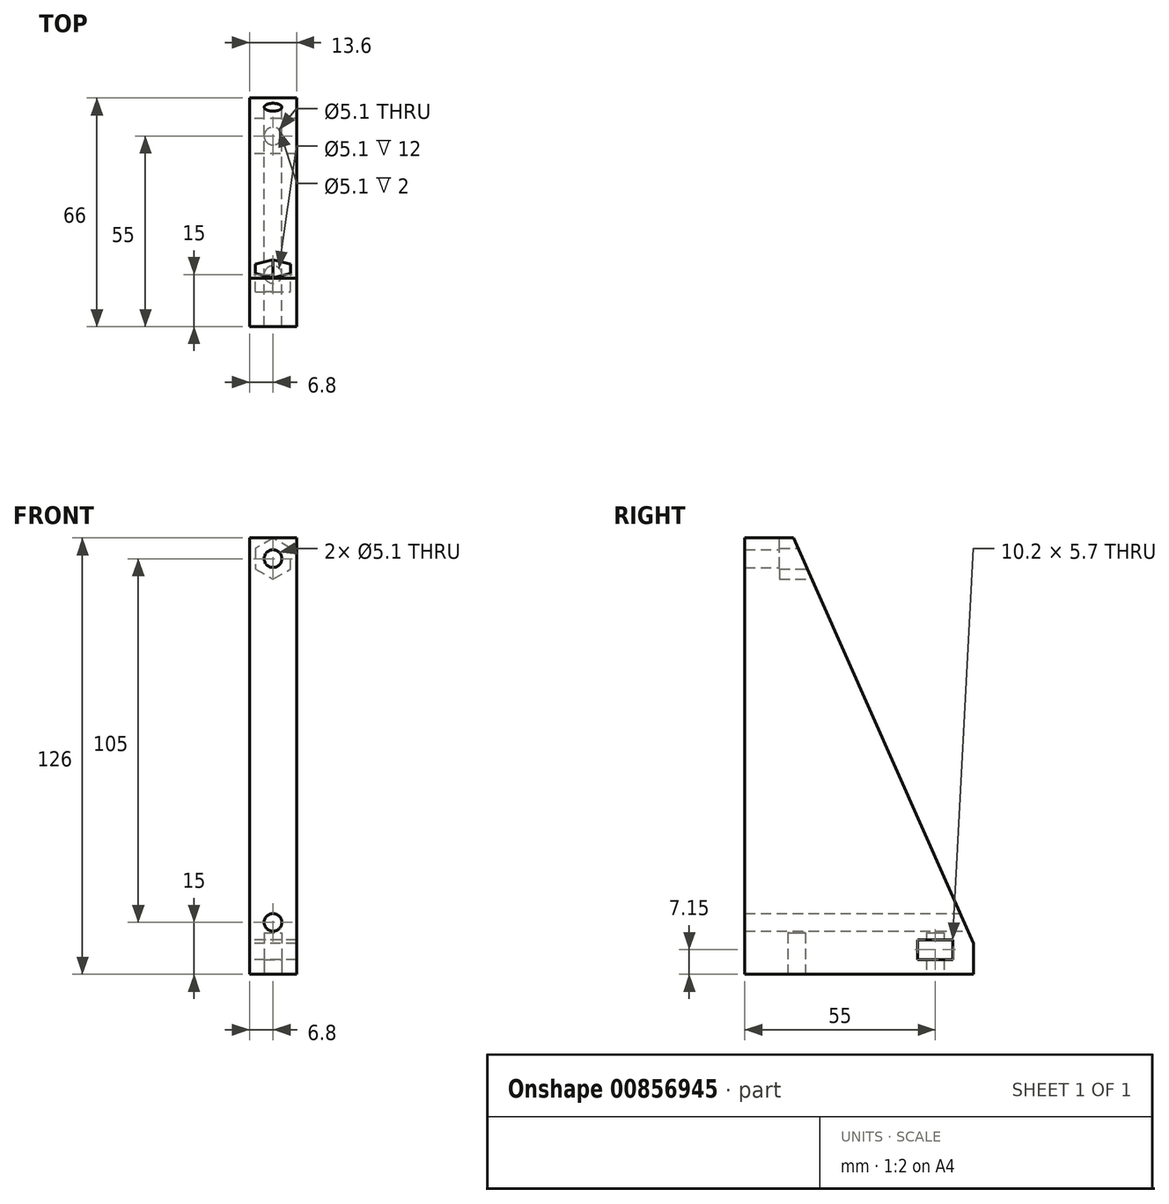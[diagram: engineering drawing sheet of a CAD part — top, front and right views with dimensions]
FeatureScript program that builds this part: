
annotation { "Feature Type Name" : "Feature", "Feature Type Description" : "" }
export const myFeature = defineFeature(function(context is Context, id is Id, definition is map)
    precondition{}
    {
        {
            var Q0;
            Q0=qCreatedBy(makeId("Right.planeOp"),FACE);
            var sketch = newSketch(context, id + "F0", { "sketchPlane" : qUnion([Q0])});
            skLineSegment(sketch, "E0", {"start": v(0, 0) * mm, "end": v(-70, 0) * mm});
            skLineSegment(sketch, "E1", {"start": v(-70, 0) * mm, "end": v(-70, 135) * mm});
            skLineSegment(sketch, "E2", {"start": v(-70, 135) * mm, "end": v(-60, 135) * mm});
            skLineSegment(sketch, "E3", {"start": v(-60, 135) * mm, "end": v(0, 0) * mm});
            skLineSegment(sketch, "E4", {"start": v(-70, 135) * mm, "end": v(-70, 126) * mm});
            skLineSegment(sketch, "E5", {"start": v(-70, 126) * mm, "end": v(-56, 126) * mm});
            skSolve(sketch);
        }
        {
            var Q0;
            Q0=qSketchRegion(id+"F0",true);
            extrude(context, id + "F1", {"entities" : qUnion([Q0]), "depth" : 13.6 * mm});
        }
        {
            var Q0;
            Q0=makeQuery(id+"F1.opExtrude","SWEPT_FACE",FACE,{"disambiguationData":[OSD([sQuery(id+"F0.wireOp",EDGE,"E1")])]});
            var sketch = newSketch(context, id + "F2", { "sketchPlane" : qUnion([Q0])});
            skLineSegment(sketch, "E6", {"start": v(6.8, 135) * mm, "end": v(6.8, 120) * mm});
            skLineSegment(sketch, "E7", {"start": v(6.8, 0) * mm, "end": v(6.8, 15) * mm});
            skPoint(sketch, "E8.0.midPoint", {"position": v(16.6, 120) * mm});
            skCircle(sketch, "E9.cCircle", {"center": v(6.8, 15) * mm, "radius": 5.1 * mm, "construction": true});
            skLineSegment(sketch, "E9.0", {"start": v(1.7, 12.06) * mm, "end": v(1.7, 17.94) * mm});
            skLineSegment(sketch, "E9.1", {"start": v(1.7, 17.94) * mm, "end": v(6.8, 20.89) * mm});
            skLineSegment(sketch, "E9.2", {"start": v(6.8, 20.89) * mm, "end": v(11.9, 17.94) * mm});
            skLineSegment(sketch, "E9.3", {"start": v(11.9, 17.94) * mm, "end": v(11.9, 12.06) * mm});
            skLineSegment(sketch, "E9.4", {"start": v(11.9, 12.06) * mm, "end": v(6.8, 9.11) * mm});
            skLineSegment(sketch, "E9.5", {"start": v(6.8, 9.11) * mm, "end": v(1.7, 12.06) * mm});
            skPoint(sketch, "E9.0.midPoint", {"position": v(1.7, 15) * mm});
            skCircle(sketch, "E10.cCircle", {"center": v(6.8, 120) * mm, "radius": 5.1 * mm, "construction": true});
            skLineSegment(sketch, "E10.0", {"start": v(1.7, 117.06) * mm, "end": v(1.7, 122.94) * mm});
            skLineSegment(sketch, "E10.1", {"start": v(1.7, 122.94) * mm, "end": v(6.8, 125.89) * mm});
            skLineSegment(sketch, "E10.2", {"start": v(6.8, 125.89) * mm, "end": v(11.9, 122.94) * mm});
            skLineSegment(sketch, "E10.3", {"start": v(11.9, 122.94) * mm, "end": v(11.9, 117.06) * mm});
            skLineSegment(sketch, "E10.4", {"start": v(11.9, 117.06) * mm, "end": v(6.8, 114.11) * mm});
            skLineSegment(sketch, "E10.5", {"start": v(6.8, 114.11) * mm, "end": v(1.7, 117.06) * mm});
            skPoint(sketch, "E10.0.midPoint", {"position": v(1.7, 120) * mm});
            skSolve(sketch);
        }
        {
            var Q0;
            Q0=sQuery(id+"F2.wireOp",VERTEX,"E7.end");
            var Q1;
            Q1=sQuery(id+"F2.wireOp",VERTEX,"E6.end");
            var Q2;
            Q2=makeQuery(id+"F1.opExtrude","SWEPT_BODY",BODY,{"disambiguationData":[OSD([sQuery(id+"F0.wireOp",EDGE,"E0"),sQuery(id+"F0.wireOp",EDGE,"E1"),sQuery(id+"F0.wireOp",EDGE,"E2"),sQuery(id+"F0.wireOp",EDGE,"E3")])]});
            hole(context, id + "F3", {"style" : HoleStyle.SIMPLE, "endStyle" : HoleEndStyle.THROUGH, "holeDiameter" : 5.1 * mm, "isTappedThrough" : true, "tappedDepth" : 12 * mm, "tapClearance" : 3, "locations" : qUnion([Q0, Q1]), "scope" : qUnion([Q2]), "startStyle" : HoleStartStyle.PART});
        }
        {
            var Q0;
            Q0=makeQuery(id+"F1.opExtrude","SWEPT_FACE",FACE,{"disambiguationData":[OSD([sQuery(id+"F0.wireOp",EDGE,"E0")])]});
            var sketch = newSketch(context, id + "F4", { "sketchPlane" : qUnion([Q0])});
            skLineSegment(sketch, "E11", {"start": v(6.8, 70) * mm, "end": v(6.8, 55) * mm});
            skLineSegment(sketch, "E12", {"start": v(6.8, 55) * mm, "end": v(6.8, 15) * mm});
            skPoint(sketch, "E12.endSnap0", {"position": v(6.8, 0) * mm});
            skCircle(sketch, "E13", {"center": v(6.8, 55) * mm, "radius": 2.55 * mm});
            skCircle(sketch, "E14", {"center": v(6.8, 15) * mm, "radius": 2.55 * mm});
            skLineSegment(sketch, "E15", {"start": v(6.8, 0) * mm, "end": v(6.8, 4) * mm});
            skLineSegment(sketch, "E16", {"start": v(6.8, 4) * mm, "end": v(13.6, 4) * mm});
            skLineSegment(sketch, "E17", {"start": v(13.6, 4) * mm, "end": v(0, 4) * mm});
            skSolve(sketch);
        }
        {
            var Q0;
            Q0=qSketchRegion(id+"F4",true);
            extrude(context, id + "F5", {"entities" : qUnion([Q0]), "operationType" : NewBodyOperationType.REMOVE, "oppositeDirection" : true, "depth" : 12 * mm});
        }
        {
            var Q0;
            Q0=makeQuery(id+"F2.imprint","IMPRINT",FACE,{"disambiguationData":[TD([[makeQuery(id+"F2.imprint","IMPRINT",EDGE,{"derivedFrom":sQuery(id+"F2.wireOp",EDGE,"E8.0")}),-1.0]])]});
            var Q1;
            Q1=makeQuery(id+"F2.imprint","IMPRINT",FACE,{"disambiguationData":[TD([[makeQuery(id+"F2.imprint","IMPRINT",EDGE,{"derivedFrom":sQuery(id+"F2.wireOp",EDGE,"E10.0")}),-1.0]])]});
            extrude(context, id + "F6", {"entities" : qUnion([Q0, Q1]), "operationType" : NewBodyOperationType.ADD, "oppositeDirection" : true, "depth" : 25 * mm});
        }
        {
            var Q0;
            Q0=makeQuery(id+"F6.opExtrude","CAP_FACE",FACE,{"disambiguationData":[OSD([sQuery(id+"F2.wireOp",EDGE,"E8.0"),sQuery(id+"F2.wireOp",EDGE,"E8.1"),sQuery(id+"F2.wireOp",EDGE,"E8.2"),sQuery(id+"F2.wireOp",EDGE,"E8.3"),sQuery(id+"F2.wireOp",EDGE,"E8.4"),sQuery(id+"F2.wireOp",EDGE,"E8.5")])],"isStart":false});
            var Q1;
            Q1=makeQuery(id+"F6.opExtrude","CAP_FACE",FACE,{"disambiguationData":[OSD([sQuery(id+"F2.wireOp",EDGE,"E10.0"),sQuery(id+"F2.wireOp",EDGE,"E10.1"),sQuery(id+"F2.wireOp",EDGE,"E10.2"),sQuery(id+"F2.wireOp",EDGE,"E10.3"),sQuery(id+"F2.wireOp",EDGE,"E10.4"),sQuery(id+"F2.wireOp",EDGE,"E10.5")])],"isStart":false});
            extrude(context, id + "F7", {"entities" : qUnion([Q0, Q1]), "operationType" : NewBodyOperationType.REMOVE, "oppositeDirection" : true, "depth" : 15 * mm});
        }
        {
            var Q0;
            Q0=sQuery(id+"F2.wireOp",VERTEX,"E6.end");
            var Q1;
            Q1=makeQuery(id+"F1.opExtrude","SWEPT_BODY",BODY,{"disambiguationData":[OSD([sQuery(id+"F0.wireOp",EDGE,"E0"),sQuery(id+"F0.wireOp",EDGE,"E1"),sQuery(id+"F0.wireOp",EDGE,"E2"),sQuery(id+"F0.wireOp",EDGE,"E3")])]});
            hole(context, id + "F8", {"style" : HoleStyle.SIMPLE, "endStyle" : HoleEndStyle.THROUGH, "holeDiameter" : 5.1 * mm, "isTappedThrough" : true, "tappedDepth" : 12 * mm, "tapClearance" : 3, "locations" : qUnion([Q0]), "scope" : qUnion([Q1]), "startStyle" : HoleStartStyle.PART});
        }
        {
            var Q0;
            Q0=makeQuery(id+"F1.opExtrude","CAP_FACE",FACE,{"disambiguationData":[OSD([sQuery(id+"F0.wireOp",EDGE,"E0"),sQuery(id+"F0.wireOp",EDGE,"E1"),sQuery(id+"F0.wireOp",EDGE,"E2"),sQuery(id+"F0.wireOp",EDGE,"E3")])],"isStart":true});
            var sketch = newSketch(context, id + "F9", { "sketchPlane" : qUnion([Q0])});
            skLineSegment(sketch, "E18", {"start": v(0, 0) * mm, "end": v(15, 0) * mm});
            skLineSegment(sketch, "E19", {"start": v(15, 0) * mm, "end": v(15, 10) * mm});
            skLineSegment(sketch, "E20", {"start": v(15, 10) * mm, "end": v(9.9, 10) * mm});
            skLineSegment(sketch, "E21", {"start": v(9.9, 10) * mm, "end": v(9.9, 4.3) * mm});
            skLineSegment(sketch, "E22", {"start": v(9.9, 4.3) * mm, "end": v(20.1, 4.3) * mm});
            skLineSegment(sketch, "E23", {"start": v(20.1, 4.3) * mm, "end": v(20.1, 10) * mm});
            skLineSegment(sketch, "E24", {"start": v(20.1, 10) * mm, "end": v(15, 10) * mm});
            skSolve(sketch);
        }
        {
            var Q0;
            {var subQ0=sQuery(id+"F9.wireOp",EDGE,"E20");Q0=makeQuery(id+"F9.imprint","IMPRINT",FACE,{"disambiguationData":[TD([[makeQuery(id+"F9.imprint","IMPRINT",EDGE,{"derivedFrom":subQ0}),1.0]])]});}
            var Q1;
            {var subQ4=sQuery(id+"F9.wireOp",EDGE,"E23");Q1=makeQuery(id+"F9.imprint","IMPRINT",FACE,{"disambiguationData":[TD([[makeQuery(id+"F9.imprint","IMPRINT",EDGE,{"derivedFrom":subQ4}),1.0]])]});}
            extrude(context, id + "F10", {"entities" : qUnion([Q0, Q1]), "operationType" : NewBodyOperationType.REMOVE, "oppositeDirection" : true, "depth" : 25 * mm});
        }
        {
            var Q0;
            {var subQ0=sQuery(id+"F4.wireOp",EDGE,"E15");Q0=makeQuery(id+"F4.imprint","IMPRINT",FACE,{"disambiguationData":[TD([[makeQuery(id+"F4.imprint","IMPRINT",EDGE,{"derivedFrom":subQ0}),-1.0]])]});}
            var Q1;
            {var subQ0=sQuery(id+"F4.wireOp",EDGE,"E15");Q1=makeQuery(id+"F4.imprint","IMPRINT",FACE,{"disambiguationData":[TD([[makeQuery(id+"F4.imprint","IMPRINT",EDGE,{"derivedFrom":subQ0}),1.0]])]});}
            extrude(context, id + "F11", {"entities" : qUnion([Q0, Q1]), "operationType" : NewBodyOperationType.REMOVE, "oppositeDirection" : true, "depth" : 25 * mm});
        }
        {
            var Q0;
            {var subQ0=sQuery(id+"F0.wireOp",EDGE,"E2");Q0=makeQuery(id+"F0.imprint","IMPRINT",FACE,{"disambiguationData":[TD([[makeQuery(id+"F0.imprint","IMPRINT",EDGE,{"derivedFrom":subQ0}),-1.0]])]});}
            extrude(context, id + "F12", {"entities" : qUnion([Q0]), "operationType" : NewBodyOperationType.REMOVE, "depth" : 25 * mm, "offsetDistance" : 25 * mm});
        }
    });
